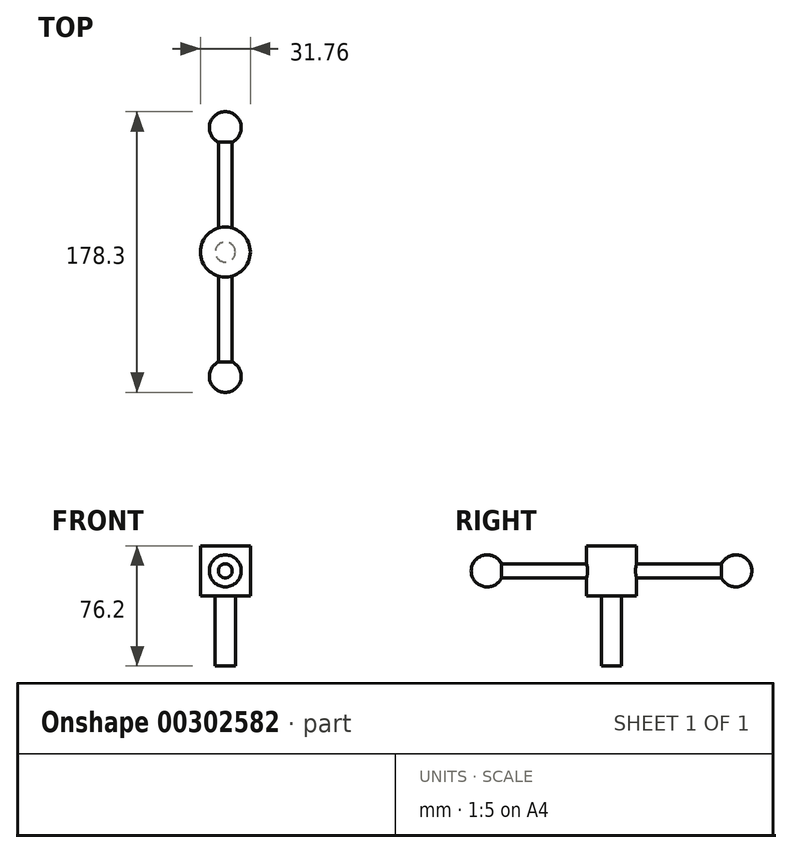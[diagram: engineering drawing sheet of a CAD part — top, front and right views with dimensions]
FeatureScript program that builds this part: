
annotation { "Feature Type Name" : "Feature", "Feature Type Description" : "" }
export const myFeature = defineFeature(function(context is Context, id is Id, definition is map)
    precondition{}
    {
        {
            var Q0;
            Q0=qCreatedBy(makeId("Top.planeOp"),FACE);
            var sketch = newSketch(context, id + "F0", { "sketchPlane" : qUnion([Q0])});
            skCircle(sketch, "E0", {"center": v(0, 0) * mm, "radius": 15.88 * mm});
            skSolve(sketch);
        }
        {
            var Q0;
            Q0 = qSketchRegion(id + "F0", true);
            extrude(context, id + "F1", {"entities" : qUnion([Q0]), "depth" : 31.75 * mm});
        }
        {
            var Q0;
            Q0=makeQuery(id+"F1.opExtrude","CAP_FACE",FACE,{"disambiguationData":[OSD([sQuery(id+"F0.wireOp",EDGE,"E0")])],"isStart":true});
            var sketch = newSketch(context, id + "F2", { "sketchPlane" : qUnion([Q0])});
            skCircle(sketch, "E1", {"center": v(0, 0) * mm, "radius": 6.35 * mm});
            skSolve(sketch);
        }
        {
            var Q0;
            Q0 = qSketchRegion(id + "F2", true);
            extrude(context, id + "F3", {"entities" : qUnion([Q0]), "operationType" : NewBodyOperationType.ADD, "depth" : 44.45 * mm});
        }
        {
            var Q0;
            Q0=qCreatedBy(makeId("Front.planeOp"),FACE);
            var sketch = newSketch(context, id + "F4", { "sketchPlane" : qUnion([Q0])});
            skLineSegment(sketch, "E2", {"start": v(0, 0) * mm, "end": v(0, 31.75) * mm, "construction": true});
            skCircle(sketch, "E3", {"center": v(0, 15.88) * mm, "radius": 4.45 * mm});
            skSolve(sketch);
        }
        {
            var Q0;
            Q0 = qSketchRegion(id + "F4", true);
            extrude(context, id + "F5", {"entities" : qUnion([Q0]), "operationType" : NewBodyOperationType.ADD, "endBound" : BoundingType.SYMMETRIC, "depth" : 139.7 * mm});
        }
        {
            var Q0;
            Q0=qCreatedBy(makeId("Right.planeOp"),FACE);
            var sketch = newSketch(context, id + "F6", { "sketchPlane" : qUnion([Q0])});
            skLineSegment(sketch, "E4.0", {"start": v(69.85, 11.43) * mm, "end": v(69.85, 20.32) * mm});
            skArc(sketch, "E5", {"start": v(89.15, 15.88) * mm, "mid": v(81.27, 25.78) * mm, "end": v(69.85, 20.32) * mm});
            skLineSegment(sketch, "E6", {"start": v(69.85, 15.88) * mm, "end": v(89.15, 15.88) * mm});
            skLineSegment(sketch, "E7", {"start": v(0, 0) * mm, "end": v(0, 49.42) * mm, "construction": true});
            skArc(sketch, "E8.MirrorCS", {"start": v(-89.15, 15.88) * mm, "mid": v(-81.27, 25.78) * mm, "end": v(-69.85, 20.32) * mm});
            skLineSegment(sketch, "E9.MirrorCS", {"start": v(-69.85, 11.43) * mm, "end": v(-69.85, 20.32) * mm});
            skLineSegment(sketch, "E10.MirrorCS", {"start": v(-69.85, 15.88) * mm, "end": v(-89.15, 15.88) * mm});
            skSolve(sketch);
        }
        {
            var Q0;
            Q0 = qSketchRegion(id + "F6", true);
            var Q1;
            Q1=sQuery(id+"F6.wireOp",EDGE,"E6");
            revolve(context, id + "F7", {"operationType" : NewBodyOperationType.ADD, "entities" : qUnion([Q0]), "axis" : qUnion([Q1]), "revolveType" : RevolveType.FULL});
        }
    });
